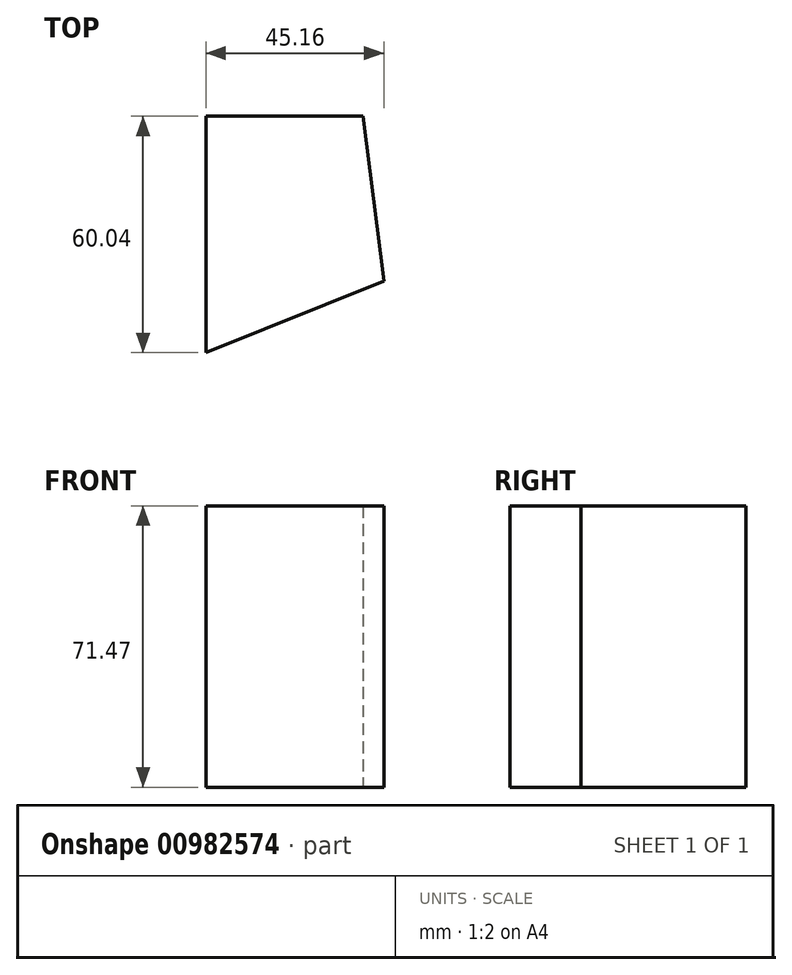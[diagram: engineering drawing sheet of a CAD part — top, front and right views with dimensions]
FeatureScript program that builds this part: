
annotation { "Feature Type Name" : "Feature", "Feature Type Description" : "" }
export const myFeature = defineFeature(function(context is Context, id is Id, definition is map)
    precondition{}
    {
        {
            var Q0;
            Q0=qCreatedBy(makeId("Top.planeOp"),FACE);
            var sketch = newSketch(context, id + "F0", { "sketchPlane" : qUnion([Q0])});
            skLineSegment(sketch, "E0", {"start": v(0, 0) * mm, "end": v(-5.34, 41.94) * mm});
            skLineSegment(sketch, "E1", {"start": v(-5.34, 41.94) * mm, "end": v(-45.16, 41.94) * mm});
            skLineSegment(sketch, "E2", {"start": v(-45.16, 41.94) * mm, "end": v(-45.16, -18.1) * mm});
            skLineSegment(sketch, "E3", {"start": v(-45.16, -18.1) * mm, "end": v(0, 0) * mm});
            skSolve(sketch);
        }
        {
            var Q0;
            Q0=makeQuery(id+"F0.imprint","IMPRINT",FACE,{"disambiguationData":[TD([[makeQuery(id+"F0.imprint","IMPRINT",EDGE,{"derivedFrom":sQuery(id+"F0.wireOp",EDGE,"E0")}),1.0]])]});
            var sketch = newSketch(context, id + "F1", { "sketchPlane" : qUnion([Q0])});
            skSolve(sketch);
        }
        {
            var Q0;
            Q0=makeQuery(id+"F1.imprint","IMPRINT",FACE,{"disambiguationData":[TD([[makeQuery(id+"F1.imprint","IMPRINT",EDGE,{"derivedFrom":makeQuery(id+"F0.imprint","IMPRINT",EDGE,{"derivedFrom":sQuery(id+"F0.wireOp",EDGE,"E0")})}),1.0]])]});
            extrude(context, id + "F2", {"entities" : qUnion([Q0]), "depth" : 71.47 * mm, "offsetDistance" : 25.4 * mm});
        }
    });
